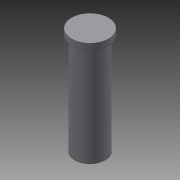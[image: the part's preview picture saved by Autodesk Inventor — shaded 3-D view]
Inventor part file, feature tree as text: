
AUTODESK INVENTOR PART (.ipt)
format: ipt  version: 2014 SP1 (Build 180222100, 222)  size: 81,408 bytes
history: native  units: in
note: dims shown in document units (in); Inventor stores cm internally (conversion verified against a paired STEP export)
features: other x1, revolve x1, chamfer x1, sketch x1, reference x1
ambient origin geometry x8: Origin, YZ Plane, XZ Plane, XY Plane, X Axis, Y Axis, Z Axis, Center Point
bodies: Solid1 (feature_tree)
feature tree (5):
  other  "Slide Catch Lever Pin"
  revolve  "Revolution1"  [1 undecoded]
  chamfer  "Chamfer1"  Angle=90.0deg  [1 undecoded]
  sketch  "Sketch1"  dims[d0=0.1955in d2=0.0385in d4=90.0deg d5=0.003in d6=0.125in d7=45.0deg]
  reference  "Reference1"
note: 2 required parameter values undecoded (feature->parameter linkage not recoverable at this tier; creation-order binding heuristic only, values carry confidence <= 0.55)